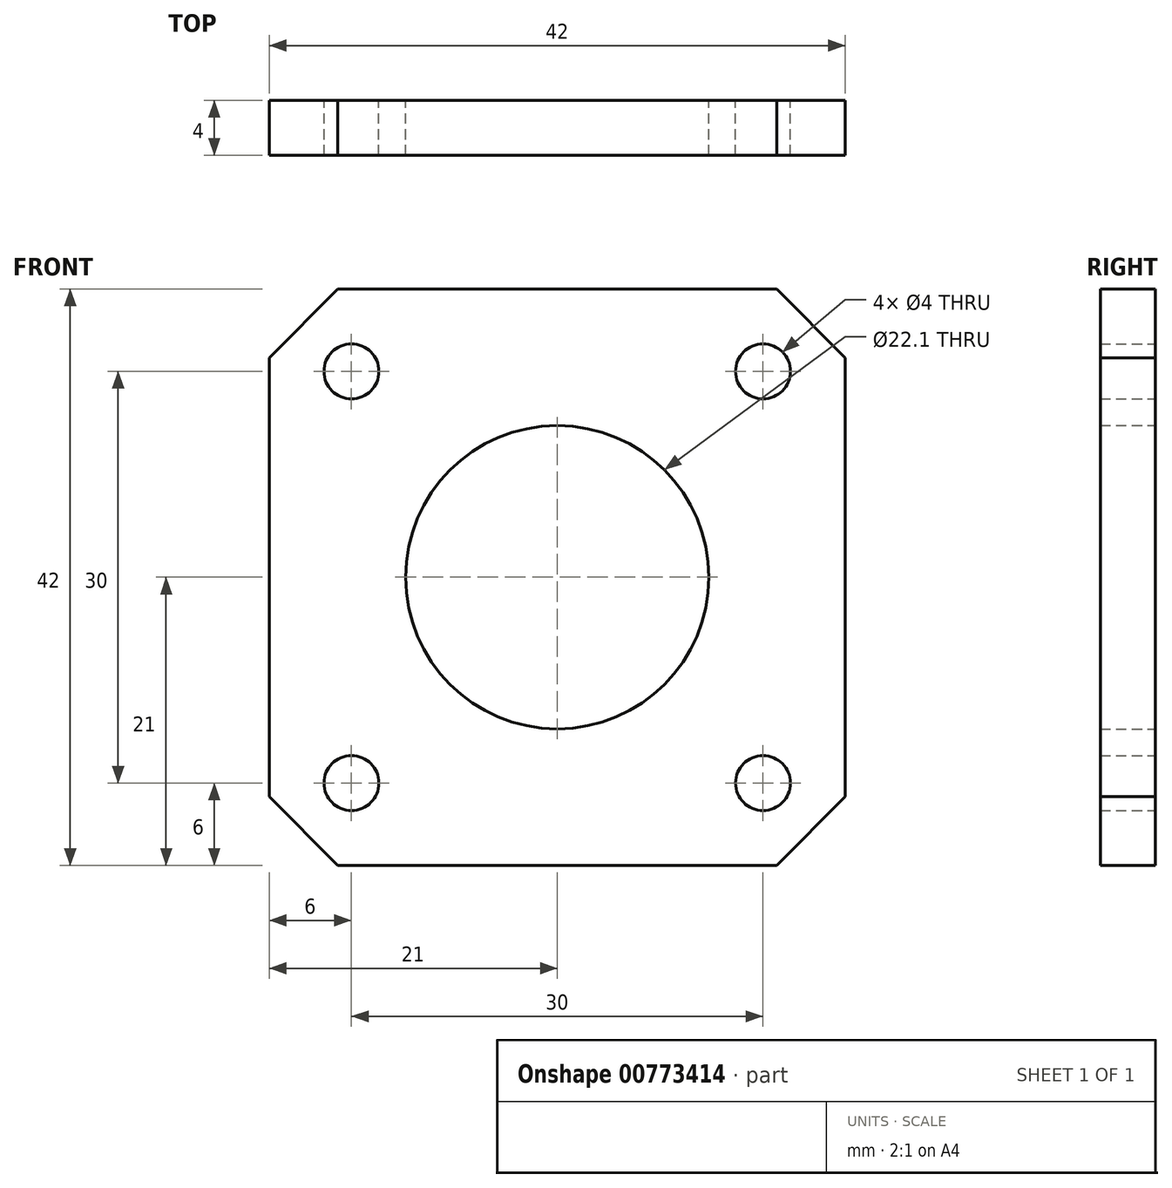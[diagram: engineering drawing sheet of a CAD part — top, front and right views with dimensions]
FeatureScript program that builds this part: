
annotation { "Feature Type Name" : "Feature", "Feature Type Description" : "" }
export const myFeature = defineFeature(function(context is Context, id is Id, definition is map)
    precondition{}
    {
        {
            var Q0;
            Q0=qCreatedBy(makeId("Front.planeOp"),FACE);
            var sketch = newSketch(context, id + "F0", { "sketchPlane" : qUnion([Q0])});
            skLineSegment(sketch, "E0.bottom", {"start": v(21, -21) * mm, "end": v(-21, -21) * mm});
            skLineSegment(sketch, "E0.top", {"start": v(21, 21) * mm, "end": v(-21, 21) * mm});
            skLineSegment(sketch, "E0.left", {"start": v(21, -21) * mm, "end": v(21, 21) * mm});
            skLineSegment(sketch, "E0.right", {"start": v(-21, -21) * mm, "end": v(-21, 21) * mm});
            skPoint(sketch, "E0.middle", {"position": v(0, 0) * mm});
            skCircle(sketch, "E1", {"center": v(0, 0) * mm, "radius": 11.05 * mm});
            skCircle(sketch, "E2", {"center": v(-15, 15) * mm, "radius": 2 * mm});
            skCircle(sketch, "E3", {"center": v(15, 15) * mm, "radius": 2 * mm});
            skCircle(sketch, "E4", {"center": v(-15, -15) * mm, "radius": 2 * mm});
            skCircle(sketch, "E5", {"center": v(15, -15) * mm, "radius": 2 * mm});
            skLineSegment(sketch, "E6.bottom", {"start": v(-15, 15) * mm, "end": v(15, 15) * mm, "construction": true});
            skLineSegment(sketch, "E6.top", {"start": v(-15, -15) * mm, "end": v(15, -15) * mm, "construction": true});
            skLineSegment(sketch, "E6.left", {"start": v(-15, 15) * mm, "end": v(-15, -15) * mm, "construction": true});
            skLineSegment(sketch, "E6.right", {"start": v(15, 15) * mm, "end": v(15, -15) * mm, "construction": true});
            skSolve(sketch);
        }
        {
            var Q0;
            Q0=makeQuery(id+"F0.imprint","IMPRINT",FACE,{"disambiguationData":[TD([[makeQuery(id+"F0.imprint","IMPRINT",EDGE,{"derivedFrom":sQuery(id+"F0.wireOp",EDGE,"E0.bottom")}),-1.0]])]});
            extrude(context, id + "F1", {"entities" : qUnion([Q0]), "depth" : 4 * mm, "offsetDistance" : 25 * mm});
        }
        {
            var Q0;
            Q0=makeQuery(id+"F1.opExtrude","SWEPT_EDGE",EDGE,{"disambiguationData":[OSD([sQuery(id+"F0.wireOp",EDGE,"E0.bottom"),sQuery(id+"F0.wireOp",EDGE,"E0.right")])]});
            chamfer(context, id + "F2", {"entities" : qUnion([Q0]), "width" : 5 * mm, "tangentPropagation" : true});
        }
        {
            var Q0;
            Q0=makeQuery(id+"F1.opExtrude","SWEPT_EDGE",EDGE,{"disambiguationData":[OSD([sQuery(id+"F0.wireOp",EDGE,"E0.top"),sQuery(id+"F0.wireOp",EDGE,"E0.right")])]});
            chamfer(context, id + "F3", {"entities" : qUnion([Q0]), "width" : 5 * mm, "tangentPropagation" : true});
        }
        {
            var Q0;
            Q0=makeQuery(id+"F1.opExtrude","SWEPT_EDGE",EDGE,{"disambiguationData":[OSD([sQuery(id+"F0.wireOp",EDGE,"E0.top"),sQuery(id+"F0.wireOp",EDGE,"E0.left")])]});
            chamfer(context, id + "F4", {"entities" : qUnion([Q0]), "width" : 5 * mm, "tangentPropagation" : true});
        }
        {
            var Q0;
            Q0=makeQuery(id+"F1.opExtrude","SWEPT_EDGE",EDGE,{"disambiguationData":[OSD([sQuery(id+"F0.wireOp",EDGE,"E0.bottom"),sQuery(id+"F0.wireOp",EDGE,"E0.left")])]});
            chamfer(context, id + "F5", {"entities" : qUnion([Q0]), "width" : 5 * mm, "tangentPropagation" : true});
        }
    });
